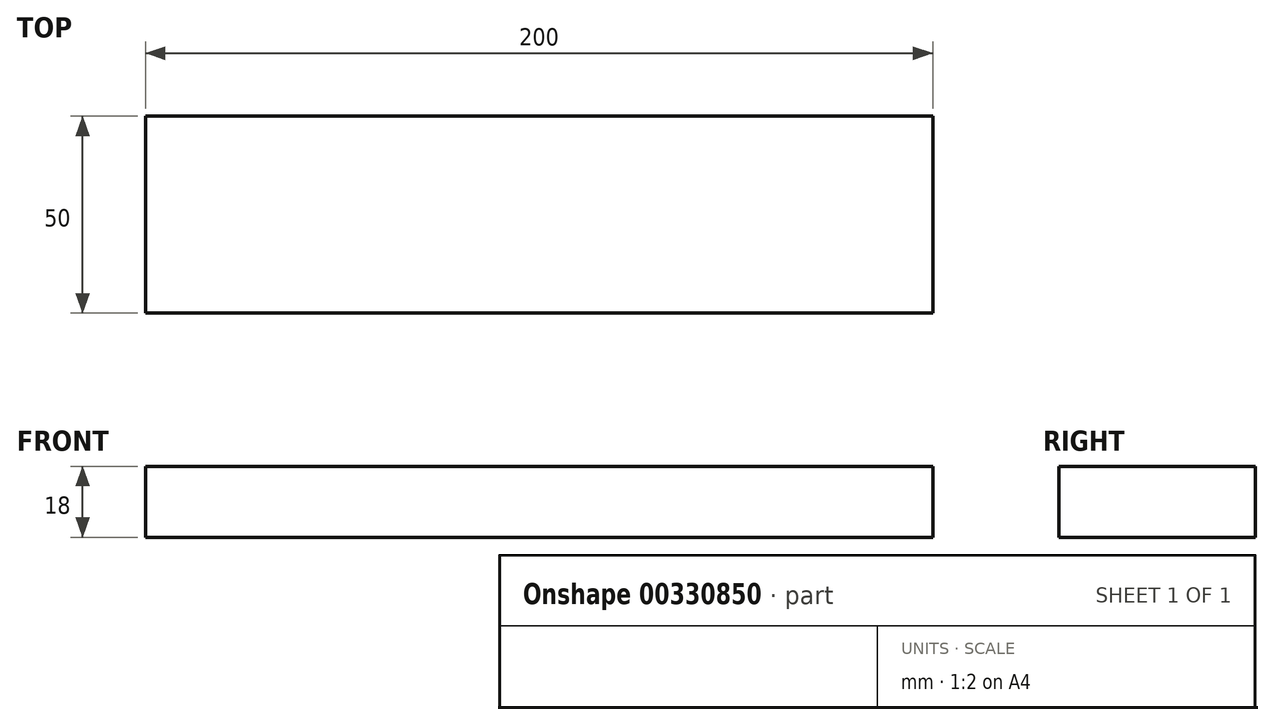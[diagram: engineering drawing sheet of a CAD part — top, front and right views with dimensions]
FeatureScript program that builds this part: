
annotation { "Feature Type Name" : "Feature", "Feature Type Description" : "" }
export const myFeature = defineFeature(function(context is Context, id is Id, definition is map)
    precondition{}
    {
        {
            var Q0;
            Q0=qCreatedBy(makeId("Top.planeOp"),FACE);
            var sketch = newSketch(context, id + "F0", { "sketchPlane" : qUnion([Q0])});
            skLineSegment(sketch, "E0.bottom", {"start": v(-46.07, 26.6) * mm, "end": v(153.93, 26.6) * mm});
            skLineSegment(sketch, "E0.top", {"start": v(-46.07, -23.4) * mm, "end": v(153.93, -23.4) * mm});
            skLineSegment(sketch, "E0.left", {"start": v(-46.07, 26.6) * mm, "end": v(-46.07, -23.4) * mm});
            skLineSegment(sketch, "E0.right", {"start": v(153.93, 26.6) * mm, "end": v(153.93, -23.4) * mm});
            skSolve(sketch);
        }
        {
            var Q0;
            Q0=makeQuery(id+"F0.imprint","IMPRINT",FACE,{"disambiguationData":[TD([[makeQuery(id+"F0.imprint","IMPRINT",EDGE,{"derivedFrom":sQuery(id+"F0.wireOp",EDGE,"E0.bottom")}),-1.0]])]});
            extrude(context, id + "F1", {"entities" : qUnion([Q0]), "depth" : 18 * mm});
        }
    });
